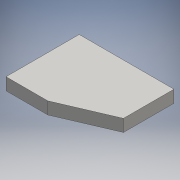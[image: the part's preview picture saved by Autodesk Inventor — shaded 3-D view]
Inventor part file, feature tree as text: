
AUTODESK INVENTOR PART (.ipt)
format: ipt  version: 2016 SP1 (Build 200210100, 210)  size: 89,600 bytes
history: native  units: mm
features: extrude x1, sketch x1
ambient origin geometry x8: Origin, YZ Plane, XZ Plane, XY Plane, X Axis, Y Axis, Z Axis, Center Point
bodies: Solid1 (feature_tree)
feature tree (2):
  extrude  "Extrusion1"  Depth=210.0mm
  sketch  "Sketch1"  dims[d0=272.0mm d1=210.0mm d2=105.0mm d3=136.0mm d4=120.0mm d5=145.0mm d6=35.0mm d7=0.0mm]
